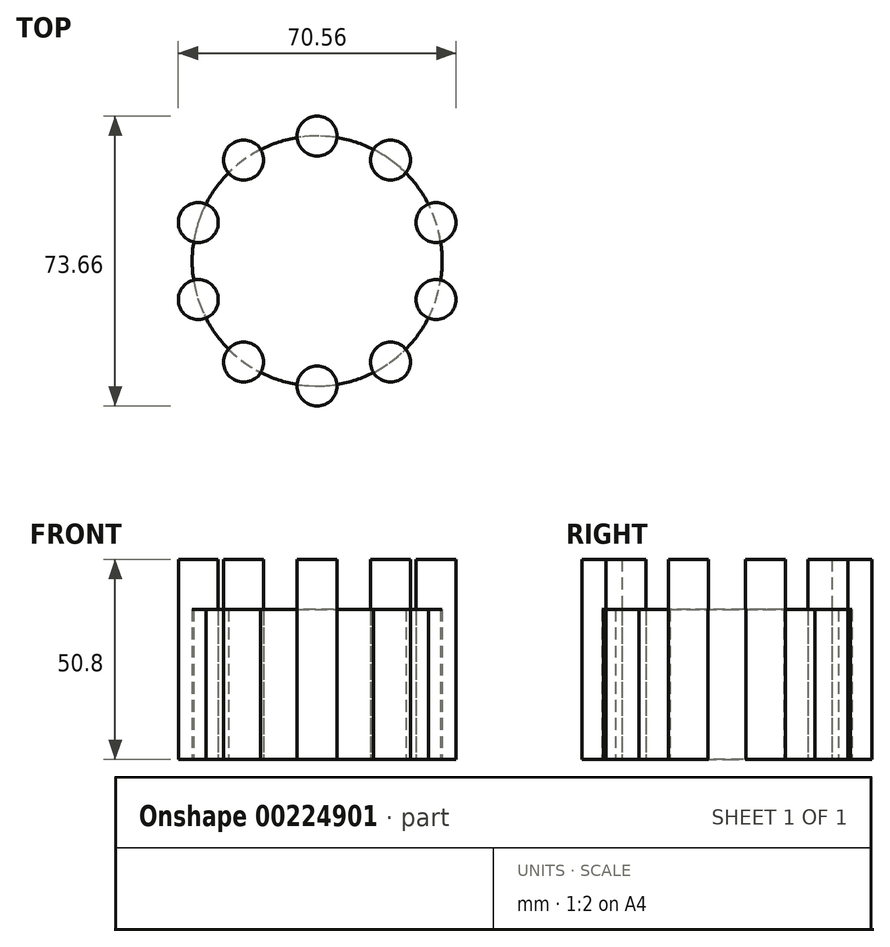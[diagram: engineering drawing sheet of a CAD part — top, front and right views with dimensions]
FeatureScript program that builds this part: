
annotation { "Feature Type Name" : "Feature", "Feature Type Description" : "" }
export const myFeature = defineFeature(function(context is Context, id is Id, definition is map)
    precondition{}
    {
        {
            var Q0;
            Q0=qCreatedBy(makeId("Top.planeOp"),FACE);
            var sketch = newSketch(context, id + "F0", { "sketchPlane" : qUnion([Q0])});
            skCircle(sketch, "E0", {"center": v(0, 0) * mm, "radius": 31.75 * mm});
            skSolve(sketch);
        }
        {
            var Q0;
            Q0=qSketchRegion(id+"F0",true);
            extrude(context, id + "F1", {"entities" : qUnion([Q0]), "depth" : 38.1 * mm});
        }
        {
            var Q0;
            Q0=qCreatedBy(makeId("Top.planeOp"),FACE);
            var sketch = newSketch(context, id + "F2", { "sketchPlane" : qUnion([Q0])});
            skCircle(sketch, "E1", {"center": v(0, 31.75) * mm, "radius": 5.08 * mm});
            skCircle(sketch, "E2.1.0", {"center": v(-18.66, 25.69) * mm, "radius": 5.08 * mm});
            skCircle(sketch, "E2.2.0", {"center": v(-30.2, 9.81) * mm, "radius": 5.08 * mm});
            skCircle(sketch, "E2.3.0", {"center": v(-30.2, -9.81) * mm, "radius": 5.08 * mm});
            skCircle(sketch, "E2.4.0", {"center": v(-18.66, -25.69) * mm, "radius": 5.08 * mm});
            skCircle(sketch, "E2.5.0", {"center": v(0, -31.75) * mm, "radius": 5.08 * mm});
            skCircle(sketch, "E2.6.0", {"center": v(18.66, -25.69) * mm, "radius": 5.08 * mm});
            skCircle(sketch, "E2.7.0", {"center": v(30.2, -9.81) * mm, "radius": 5.08 * mm});
            skCircle(sketch, "E2.8.0", {"center": v(30.2, 9.81) * mm, "radius": 5.08 * mm});
            skCircle(sketch, "E2.9.0", {"center": v(18.66, 25.69) * mm, "radius": 5.08 * mm});
            skPoint(sketch, "E2.center", {"position": v(0, 0) * mm});
            skSolve(sketch);
        }
        {
            var Q0;
            Q0=qSketchRegion(id+"F2",true);
            extrude(context, id + "F3", {"entities" : qUnion([Q0]), "depth" : 50.8 * mm});
        }
        {
            var Q0;
            Q0=makeQuery(id+"F3.opExtrude","SWEPT_BODY",BODY,{"disambiguationData":[OSD([sQuery(id+"F2.wireOp",EDGE,"E2.6.0")])]});
            var Q1;
            Q1=makeQuery(id+"F1.opExtrude","SWEPT_BODY",BODY,{"disambiguationData":[OSD([sQuery(id+"F0.wireOp",EDGE,"E0")])]});
            booleanBodies(context, id + "F4", {"operationType" : BooleanOperationType.INTERSECTION, "tools" : qUnion([Q0, Q1]), "keepTools" : true});
        }
        {
            var Q0;
            Q0=makeQuery(id+"F3.opExtrude","SWEPT_BODY",BODY,{"disambiguationData":[OSD([sQuery(id+"F2.wireOp",EDGE,"E2.7.0")])]});
            var Q1;
            Q1=makeQuery(id+"F1.opExtrude","SWEPT_BODY",BODY,{"disambiguationData":[OSD([sQuery(id+"F0.wireOp",EDGE,"E0")])]});
            booleanBodies(context, id + "F5", {"operationType" : BooleanOperationType.INTERSECTION, "tools" : qUnion([Q0, Q1]), "keepTools" : true});
        }
        {
            var Q0;
            Q0=makeQuery(id+"F3.opExtrude","SWEPT_BODY",BODY,{"disambiguationData":[OSD([sQuery(id+"F2.wireOp",EDGE,"E2.8.0")])]});
            var Q1;
            Q1=makeQuery(id+"F1.opExtrude","SWEPT_BODY",BODY,{"disambiguationData":[OSD([sQuery(id+"F0.wireOp",EDGE,"E0")])]});
            booleanBodies(context, id + "F6", {"operationType" : BooleanOperationType.INTERSECTION, "tools" : qUnion([Q0, Q1]), "keepTools" : true});
        }
        {
            var Q0;
            Q0=makeQuery(id+"F1.opExtrude","SWEPT_BODY",BODY,{"disambiguationData":[OSD([sQuery(id+"F0.wireOp",EDGE,"E0")])]});
            var Q1;
            Q1=makeQuery(id+"F3.opExtrude","SWEPT_BODY",BODY,{"disambiguationData":[OSD([sQuery(id+"F2.wireOp",EDGE,"E2.9.0")])]});
            booleanBodies(context, id + "F7", {"operationType" : BooleanOperationType.INTERSECTION, "tools" : qUnion([Q0, Q1]), "keepTools" : true});
        }
        {
            var Q0;
            Q0=makeQuery(id+"F3.opExtrude","SWEPT_BODY",BODY,{"disambiguationData":[OSD([sQuery(id+"F2.wireOp",EDGE,"E1")])]});
            var Q1;
            Q1=makeQuery(id+"F1.opExtrude","SWEPT_BODY",BODY,{"disambiguationData":[OSD([sQuery(id+"F0.wireOp",EDGE,"E0")])]});
            booleanBodies(context, id + "F8", {"operationType" : BooleanOperationType.INTERSECTION, "tools" : qUnion([Q0, Q1]), "keepTools" : true});
        }
        {
            var Q0;
            Q0=makeQuery(id+"F1.opExtrude","SWEPT_BODY",BODY,{"disambiguationData":[OSD([sQuery(id+"F0.wireOp",EDGE,"E0")])]});
            var Q1;
            Q1=makeQuery(id+"F3.opExtrude","SWEPT_BODY",BODY,{"disambiguationData":[OSD([sQuery(id+"F2.wireOp",EDGE,"E2.1.0")])]});
            booleanBodies(context, id + "F9", {"operationType" : BooleanOperationType.INTERSECTION, "tools" : qUnion([Q0, Q1]), "keepTools" : true});
        }
        {
            var Q0;
            Q0=makeQuery(id+"F1.opExtrude","SWEPT_BODY",BODY,{"disambiguationData":[OSD([sQuery(id+"F0.wireOp",EDGE,"E0")])]});
            var Q1;
            Q1=makeQuery(id+"F3.opExtrude","SWEPT_BODY",BODY,{"disambiguationData":[OSD([sQuery(id+"F2.wireOp",EDGE,"E2.2.0")])]});
            booleanBodies(context, id + "F10", {"operationType" : BooleanOperationType.INTERSECTION, "tools" : qUnion([Q0, Q1]), "keepTools" : true});
        }
        {
            var Q0;
            Q0=makeQuery(id+"F3.opExtrude","SWEPT_BODY",BODY,{"disambiguationData":[OSD([sQuery(id+"F2.wireOp",EDGE,"E2.3.0")])]});
            var Q1;
            Q1=makeQuery(id+"F1.opExtrude","SWEPT_BODY",BODY,{"disambiguationData":[OSD([sQuery(id+"F0.wireOp",EDGE,"E0")])]});
            booleanBodies(context, id + "F11", {"operationType" : BooleanOperationType.INTERSECTION, "tools" : qUnion([Q0, Q1]), "keepTools" : true});
        }
        {
            var Q0;
            Q0=makeQuery(id+"F3.opExtrude","SWEPT_BODY",BODY,{"disambiguationData":[OSD([sQuery(id+"F2.wireOp",EDGE,"E2.4.0")])]});
            var Q1;
            Q1=makeQuery(id+"F1.opExtrude","SWEPT_BODY",BODY,{"disambiguationData":[OSD([sQuery(id+"F0.wireOp",EDGE,"E0")])]});
            booleanBodies(context, id + "F12", {"operationType" : BooleanOperationType.INTERSECTION, "tools" : qUnion([Q0, Q1]), "keepTools" : true});
        }
        {
            var Q0;
            Q0=makeQuery(id+"F3.opExtrude","SWEPT_BODY",BODY,{"disambiguationData":[OSD([sQuery(id+"F2.wireOp",EDGE,"E2.5.0")])]});
            var Q1;
            Q1=makeQuery(id+"F1.opExtrude","SWEPT_BODY",BODY,{"disambiguationData":[OSD([sQuery(id+"F0.wireOp",EDGE,"E0")])]});
            booleanBodies(context, id + "F13", {"operationType" : BooleanOperationType.INTERSECTION, "tools" : qUnion([Q0, Q1]), "keepTools" : true});
        }
    });
